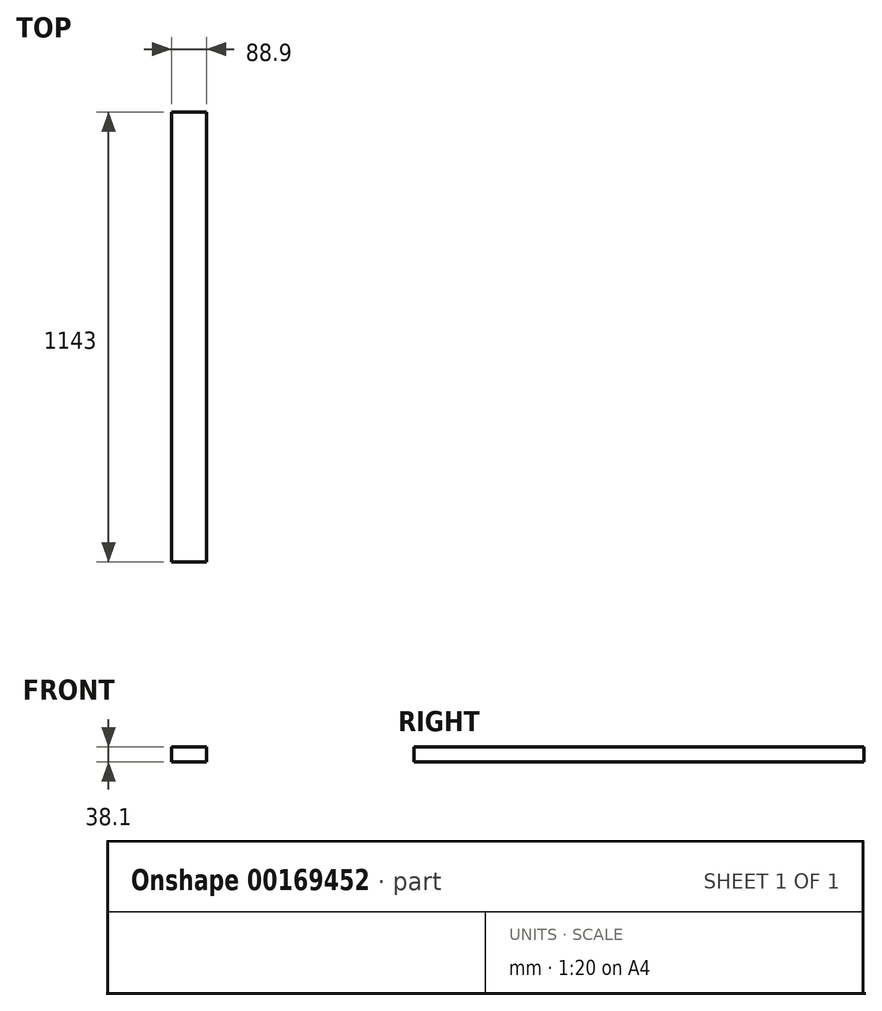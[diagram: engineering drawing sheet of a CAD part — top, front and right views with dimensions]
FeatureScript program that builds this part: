
annotation { "Feature Type Name" : "Feature", "Feature Type Description" : "" }
export const myFeature = defineFeature(function(context is Context, id is Id, definition is map)
    precondition{}
    {
        {
            var Q0;
            Q0=qCreatedBy(makeId("Front.planeOp"),FACE);
            var sketch = newSketch(context, id + "F0", { "sketchPlane" : qUnion([Q0])});
            skLineSegment(sketch, "E0.bottom", {"start": v(0, 0) * mm, "end": v(88.9, 0) * mm});
            skLineSegment(sketch, "E0.top", {"start": v(0, -38.1) * mm, "end": v(88.9, -38.1) * mm});
            skLineSegment(sketch, "E0.left", {"start": v(0, 0) * mm, "end": v(0, -38.1) * mm});
            skLineSegment(sketch, "E0.right", {"start": v(88.9, 0) * mm, "end": v(88.9, -38.1) * mm});
            skSolve(sketch);
        }
        {
            var Q0;
            Q0=qSketchRegion(id+"F0",true);
            extrude(context, id + "F1", {"entities" : qUnion([Q0]), "depth" : 1143 * mm});
        }
    });
